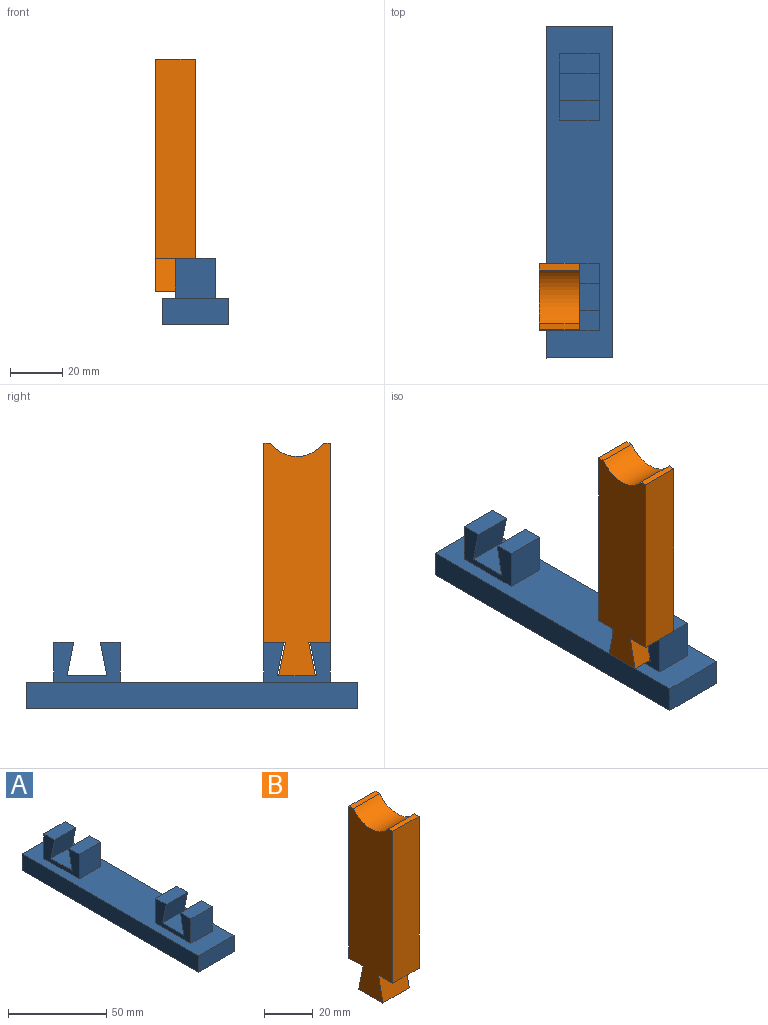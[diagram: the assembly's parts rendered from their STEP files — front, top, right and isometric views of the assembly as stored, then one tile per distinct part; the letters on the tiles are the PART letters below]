
ASSEMBLY  parts=2 mates=1
PART A: 24 faces, bbox 25.4x127x25.4 mm
  f0: plane 15.24x7.62mm, normal (0,0,1), area 116.1mm2, adj f2,f3,f10,f21
  f1: plane 15.24x7.62mm, normal (0,0,1), area 116.1mm2, adj f14,f15,f16,f20
  f2: plane 25.4x15.24mm, normal (1,0,0), area 225.8mm2, adj f0,f8,f10,f11,f12,f21,f22,f23
  f3: plane 25.4x15.24mm, normal (-1,0,0), area 225.8mm2, adj f0,f8,f10,f11,f12,f21,f22,f23
  f4: plane 127x10.16mm, normal (1,0,0), area 1290.3mm2, adj f5,f7,f8,f9
  f5: plane 25.4x10.16mm, normal (0,1,0), area 258.1mm2, adj f4,f6,f8,f9
  f6: plane 127x10.16mm, normal (-1,0,0), area 1290.3mm2, adj f5,f7,f8,f9
  f7: plane 25.4x10.16mm, normal (0,-1,0), area 258.1mm2, adj f4,f6,f8,f9
  f8: plane 127x25.4mm, normal (0,0,1), area 2451.6mm2, adj f2,f3,f4,f5,f6,f7,f10,f11
  f9: plane 127x25.4mm, normal (0,0,-1), area 3225.8mm2, adj f4,f5,f6,f7
  f10: plane 15.24x15.24mm, normal (0,1,0), area 232.3mm2, adj f0,f2,f3,f8
  f11: plane 15.24x15.24mm, normal (0,-1,0), area 232.3mm2, adj f2,f3,f8,f12
  f12: plane 15.24x7.62mm, normal (0,0,1), area 116.1mm2, adj f2,f3,f11,f22
  f13: plane 15.24x15.24mm, normal (0,-1,0), area 232.3mm2, adj f8,f14,f16,f17
  f14: plane 25.4x15.24mm, normal (1,0,0), area 225.8mm2, adj f1,f8,f13,f15,f17,f18,f19,f20
  f15: plane 15.24x15.24mm, normal (0,1,0), area 232.3mm2, adj f1,f8,f14,f16
  f16: plane 25.4x15.24mm, normal (-1,0,0), area 225.8mm2, adj f1,f8,f13,f15,f17,f18,f19,f20
  f17: plane 15.24x7.62mm, normal (0,0,1), area 116.1mm2, adj f13,f14,f16,f18
  f18: plane 15.24x12.7mm, normal (0,0.98,-0.2), area 197.4mm2, adj f14,f16,f17,f19
  f19: plane 15.24x15.24mm, normal (0,0,1), area 232.3mm2, adj f14,f16,f18,f20
  f20: plane 15.24x12.7mm, normal (0,-0.98,-0.2), area 197.4mm2, adj f1,f14,f16,f19
  f21: plane 15.24x12.7mm, normal (0,-0.98,-0.2), area 197.4mm2, adj f0,f2,f3,f23
  f22: plane 15.24x12.7mm, normal (0,0.98,-0.2), area 197.4mm2, adj f2,f3,f12,f23
  f23: plane 15.24x15.24mm, normal (0,0,1), area 232.3mm2, adj f2,f3,f21,f22
PART B: 12 faces, bbox 15.2x25.4x88.9 mm
  f0: plane 15.24x2.54mm, normal (0,0,1), area 38.7mm2, adj f4,f5,f10,f11
  f1: plane 15.24x13.97mm, normal (0,0,-1), area 212.9mm2, adj f2,f3,f4,f5
  f2: plane 15.24x12.7mm, normal (0,0.98,0.2), area 197.4mm2, adj f1,f4,f5,f7
  f3: plane 15.24x12.7mm, normal (0,-0.98,0.2), area 197.4mm2, adj f1,f4,f5,f6
  f4: plane 88.9x25.4mm, normal (1,0,0), area 2008.5mm2, adj f0,f1,f2,f3,f6,f7,f8,f9
  f5: plane 88.9x25.4mm, normal (-1,0,0), area 2008.5mm2, adj f0,f1,f2,f3,f6,f7,f8,f9
  f6: plane 15.24x8.26mm, normal (0,0,-1), area 125.8mm2, adj f3,f4,f5,f10
  f7: plane 15.24x8.26mm, normal (0,0,-1), area 125.8mm2, adj f2,f4,f5,f8
  f8: plane 76.2x15.24mm, normal (0,1,0), area 1161.3mm2, adj f4,f5,f7,f9
  f9: plane 15.24x2.54mm, normal (0,0,1), area 38.7mm2, adj f4,f5,f8,f11
  f10: plane 76.2x15.24mm, normal (0,-1,0), area 1161.3mm2, adj f0,f4,f5,f6
  f11: cylinder r=12.7mm len=20.32mm, axis (1,0,0), area 359mm2, adj f0,f4,f5,f9
PLACE A t=(-58.92,-13.61,5.92)mm
PLACE B rot(axis=(0,0.55,0.83),0deg) t=(-66.54,-53.8,31.32)mm
MATE fastened B.f1 <-> A.f19  axis (0,0,-1) through (-66.54,-53.8,18.62)mm
